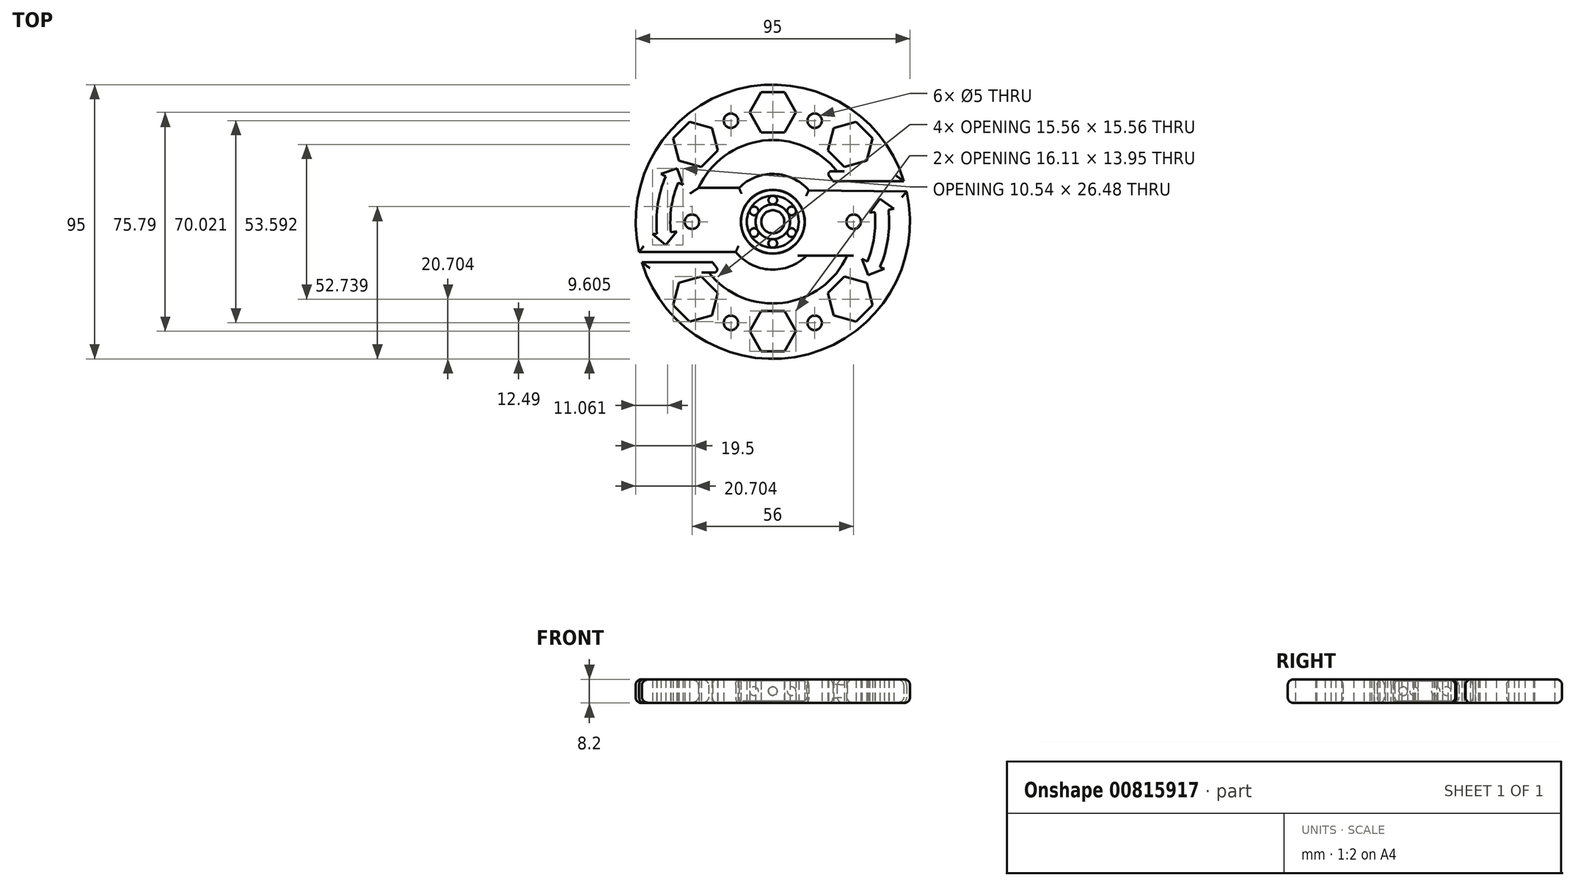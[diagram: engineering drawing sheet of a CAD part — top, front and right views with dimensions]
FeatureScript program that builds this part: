
annotation { "Feature Type Name" : "Feature", "Feature Type Description" : "" }
export const myFeature = defineFeature(function(context is Context, id is Id, definition is map)
    precondition{}
    {
        {
            var Q0;
            Q0=qCreatedBy(makeId("Top.planeOp"),FACE);
            var sketch = newSketch(context, id + "F0", { "sketchPlane" : qUnion([Q0])});
            skArc(sketch, "E0", {"start": v(45.38, 14.04) * mm, "mid": v(-10.46, 46.33) * mm, "end": v(-47, -6.81) * mm});
            skLineSegment(sketch, "E1.top", {"start": v(-45.38, -14.04) * mm, "end": v(-24.56, -14.04) * mm});
            skCircle(sketch, "E2", {"center": v(0, 0) * mm, "radius": 11.07 * mm});
            skArc(sketch, "E3", {"start": v(22.24, 17.5) * mm, "mid": v(-3.38, 28.09) * mm, "end": v(-25.75, 11.72) * mm});
            skArc(sketch, "E4.trimOffspring", {"start": v(-22.2, -17.54) * mm, "mid": v(3.4, -28.08) * mm, "end": v(25.75, -11.72) * mm});
            skArc(sketch, "E5.trimOffspring", {"start": v(-45.38, -14.04) * mm, "mid": v(10.5, -46.32) * mm, "end": v(47, 6.9) * mm});
            skLineSegment(sketch, "E6.trimOffspring", {"start": v(24.59, 14) * mm, "end": v(45.38, 14.04) * mm});
            skPoint(sketch, "E7.trimOffspring.end.orphan", {"position": v(45.38, -14.04) * mm});
            skPoint(sketch, "E1.bottom.start.orphan", {"position": v(-45.38, 14.04) * mm});
            skPoint(sketch, "E8.orphan", {"position": v(47, -6.9) * mm});
            skPoint(sketch, "E9.orphan", {"position": v(-47, 6.81) * mm});
            skArc(sketch, "E10", {"start": v(-12.86, -10.46) * mm, "mid": v(-0.85, -16.55) * mm, "end": v(11.72, -11.72) * mm});
            skArc(sketch, "E11.trimOffspring", {"start": v(12.47, 10.92) * mm, "mid": v(0.55, 16.57) * mm, "end": v(-11.72, 11.72) * mm});
            skLineSegment(sketch, "E12.trimOffspring", {"start": v(-8.7, 6.85) * mm, "end": v(8.59, 7) * mm});
            skLineSegment(sketch, "E13.trimOffspring", {"start": v(-8.7, -6.85) * mm, "end": v(8.69, -6.87) * mm});
            skLineSegment(sketch, "E14", {"start": v(-7.83, 7.83) * mm, "end": v(-6.87, 6.87) * mm});
            skLineSegment(sketch, "E15", {"start": v(6.87, -6.87) * mm, "end": v(7.83, -7.83) * mm});
            skLineSegment(sketch, "E16", {"start": v(-11.72, 11.72) * mm, "end": v(-25.75, 11.72) * mm});
            skLineSegment(sketch, "E17", {"start": v(11.72, -11.72) * mm, "end": v(11.72, -11.72) * mm});
            skArc(sketch, "E18", {"start": v(20.88, 14) * mm, "mid": v(19.54, 15.8) * mm, "end": v(18.05, 17.5) * mm});
            skLineSegment(sketch, "E19", {"start": v(-24.56, -14.04) * mm, "end": v(-20.85, -14.04) * mm});
            skLineSegment(sketch, "E20", {"start": v(24.59, 14) * mm, "end": v(20.88, 14) * mm});
            skLineSegment(sketch, "E21", {"start": v(22.24, 17.5) * mm, "end": v(18.05, 17.5) * mm});
            skLineSegment(sketch, "E22", {"start": v(-22.2, -17.54) * mm, "end": v(-18, -17.54) * mm});
            skArc(sketch, "E23.trimOffspring", {"start": v(-20.85, -14.04) * mm, "mid": v(-19.5, -15.85) * mm, "end": v(-18, -17.54) * mm});
            skLineSegment(sketch, "E24", {"start": v(0, 0) * mm, "end": v(0, 16.57) * mm, "construction": true});
            skLineSegment(sketch, "E25", {"start": v(-6.87, 6.87) * mm, "end": v(-11.72, 11.72) * mm, "construction": true});
            skLineSegment(sketch, "E26", {"start": v(0, 0) * mm, "end": v(11.72, 11.72) * mm, "construction": true});
            skLineSegment(sketch, "E27", {"start": v(6.87, -6.87) * mm, "end": v(11.72, -11.72) * mm, "construction": true});
            skLineSegment(sketch, "E28", {"start": v(0, 0) * mm, "end": v(0, -16.57) * mm, "construction": true});
            skLineSegment(sketch, "E29", {"start": v(0, 0) * mm, "end": v(-11.72, -11.72) * mm, "construction": true});
            skLineSegment(sketch, "E30.trimOffspring", {"start": v(-20, 20) * mm, "end": v(-33.59, 33.59) * mm, "construction": true});
            skLineSegment(sketch, "E31.trimOffspring", {"start": v(0, 28.29) * mm, "end": v(0, 47.5) * mm, "construction": true});
            skLineSegment(sketch, "E32.trimOffspring", {"start": v(20, 20) * mm, "end": v(33.59, 33.59) * mm, "construction": true});
            skLineSegment(sketch, "E33.trimOffspring", {"start": v(20, -20) * mm, "end": v(33.59, -33.59) * mm, "construction": true});
            skLineSegment(sketch, "E34.trimOffspring", {"start": v(0, -28.29) * mm, "end": v(0, -47.5) * mm, "construction": true});
            skLineSegment(sketch, "E35.trimOffspring", {"start": v(-20, -20) * mm, "end": v(-33.59, -33.59) * mm, "construction": true});
            skPoint(sketch, "E36", {"position": v(0, 37.9) * mm});
            skPoint(sketch, "E37", {"position": v(-26.8, 26.8) * mm});
            skPoint(sketch, "E38", {"position": v(26.8, 26.8) * mm});
            skPoint(sketch, "E39", {"position": v(26.8, -26.8) * mm});
            skPoint(sketch, "E40", {"position": v(0, -37.9) * mm});
            skPoint(sketch, "E41", {"position": v(-26.8, -26.8) * mm});
            skLineSegment(sketch, "E42.0", {"start": v(-32.5, 21.1) * mm, "end": v(-34.58, 28.88) * mm});
            skLineSegment(sketch, "E42.1", {"start": v(-34.58, 28.88) * mm, "end": v(-28.88, 34.58) * mm});
            skLineSegment(sketch, "E42.2", {"start": v(-28.88, 34.58) * mm, "end": v(-21.1, 32.5) * mm});
            skLineSegment(sketch, "E42.3", {"start": v(-21.1, 32.5) * mm, "end": v(-19.02, 24.71) * mm});
            skLineSegment(sketch, "E42.4", {"start": v(-19.02, 24.71) * mm, "end": v(-24.71, 19.02) * mm});
            skLineSegment(sketch, "E42.5", {"start": v(-24.71, 19.02) * mm, "end": v(-32.5, 21.1) * mm});
            skLineSegment(sketch, "E43.0", {"start": v(21.1, -32.5) * mm, "end": v(19.02, -24.71) * mm});
            skLineSegment(sketch, "E43.1", {"start": v(19.02, -24.71) * mm, "end": v(24.71, -19.02) * mm});
            skLineSegment(sketch, "E43.2", {"start": v(24.71, -19.02) * mm, "end": v(32.5, -21.1) * mm});
            skLineSegment(sketch, "E43.3", {"start": v(32.5, -21.1) * mm, "end": v(34.58, -28.88) * mm});
            skLineSegment(sketch, "E43.4", {"start": v(34.58, -28.88) * mm, "end": v(28.88, -34.58) * mm});
            skLineSegment(sketch, "E43.5", {"start": v(28.88, -34.58) * mm, "end": v(21.1, -32.5) * mm});
            skLineSegment(sketch, "E44.0", {"start": v(-8.05, 37.9) * mm, "end": v(-4.03, 44.87) * mm});
            skLineSegment(sketch, "E44.1", {"start": v(-4.03, 44.87) * mm, "end": v(4.03, 44.87) * mm});
            skLineSegment(sketch, "E44.2", {"start": v(4.03, 44.87) * mm, "end": v(8.05, 37.9) * mm});
            skLineSegment(sketch, "E44.3", {"start": v(8.05, 37.9) * mm, "end": v(4.03, 30.92) * mm});
            skLineSegment(sketch, "E44.4", {"start": v(4.03, 30.92) * mm, "end": v(-4.03, 30.92) * mm});
            skLineSegment(sketch, "E44.5", {"start": v(-4.03, 30.92) * mm, "end": v(-8.05, 37.9) * mm});
            skLineSegment(sketch, "E45.0", {"start": v(-8.05, -37.9) * mm, "end": v(-4.03, -30.92) * mm});
            skLineSegment(sketch, "E45.1", {"start": v(-4.03, -30.92) * mm, "end": v(4.03, -30.92) * mm});
            skLineSegment(sketch, "E45.2", {"start": v(4.03, -30.92) * mm, "end": v(8.05, -37.9) * mm});
            skLineSegment(sketch, "E45.3", {"start": v(8.05, -37.9) * mm, "end": v(4.03, -44.87) * mm});
            skLineSegment(sketch, "E45.4", {"start": v(4.03, -44.87) * mm, "end": v(-4.03, -44.87) * mm});
            skLineSegment(sketch, "E45.5", {"start": v(-4.03, -44.87) * mm, "end": v(-8.05, -37.9) * mm});
            skLineSegment(sketch, "E46.0", {"start": v(-32.5, -21.1) * mm, "end": v(-24.71, -19.02) * mm});
            skLineSegment(sketch, "E46.1", {"start": v(-24.71, -19.02) * mm, "end": v(-19.02, -24.71) * mm});
            skLineSegment(sketch, "E46.2", {"start": v(-19.02, -24.71) * mm, "end": v(-21.1, -32.5) * mm});
            skLineSegment(sketch, "E46.3", {"start": v(-21.1, -32.5) * mm, "end": v(-28.88, -34.58) * mm});
            skLineSegment(sketch, "E46.4", {"start": v(-28.88, -34.58) * mm, "end": v(-34.58, -28.88) * mm});
            skLineSegment(sketch, "E46.5", {"start": v(-34.58, -28.88) * mm, "end": v(-32.5, -21.1) * mm});
            skLineSegment(sketch, "E47.0", {"start": v(21.1, 32.5) * mm, "end": v(28.88, 34.58) * mm});
            skLineSegment(sketch, "E47.1", {"start": v(28.88, 34.58) * mm, "end": v(34.58, 28.88) * mm});
            skLineSegment(sketch, "E47.2", {"start": v(34.58, 28.88) * mm, "end": v(32.5, 21.1) * mm});
            skLineSegment(sketch, "E47.3", {"start": v(32.5, 21.1) * mm, "end": v(24.71, 19.02) * mm});
            skLineSegment(sketch, "E47.4", {"start": v(24.71, 19.02) * mm, "end": v(19.02, 24.71) * mm});
            skLineSegment(sketch, "E47.5", {"start": v(19.02, 24.71) * mm, "end": v(21.1, 32.5) * mm});
            skArc(sketch, "E48", {"start": v(-45.38, -14.04) * mm, "mid": v(10.5, -46.32) * mm, "end": v(47, 6.9) * mm, "construction": true});
            skArc(sketch, "E49", {"start": v(-47, -6.81) * mm, "mid": v(-46.7, -8.64) * mm, "end": v(-46.33, -10.46) * mm});
            skPoint(sketch, "E50", {"position": v(-46.33, -10.46) * mm});
            skArc(sketch, "E51", {"start": v(45.38, 14.04) * mm, "mid": v(-10.46, 46.33) * mm, "end": v(-47, -6.81) * mm, "construction": true});
            skArc(sketch, "E52", {"start": v(47, 6.9) * mm, "mid": v(46.7, 8.71) * mm, "end": v(46.32, 10.5) * mm});
            skPoint(sketch, "E53", {"position": v(46.32, 10.5) * mm});
            skLineSegment(sketch, "E54", {"start": v(-46.33, -10.46) * mm, "end": v(-36.42, -10.46) * mm});
            skLineSegment(sketch, "E55", {"start": v(46.32, 10.5) * mm, "end": v(12.47, 10.92) * mm});
            skPoint(sketch, "E56", {"position": v(-114.88, 3.23) * mm});
            skLineSegment(sketch, "E57.0", {"start": v(-114.88, 9.7) * mm, "end": v(-109.28, 6.47) * mm});
            skLineSegment(sketch, "E57.1", {"start": v(-109.28, 6.47) * mm, "end": v(-109.28, 0) * mm});
            skLineSegment(sketch, "E57.2", {"start": v(-109.28, 0) * mm, "end": v(-114.88, -3.23) * mm});
            skLineSegment(sketch, "E57.3", {"start": v(-114.88, -3.23) * mm, "end": v(-120.48, 0) * mm});
            skLineSegment(sketch, "E57.4", {"start": v(-120.48, 0) * mm, "end": v(-120.48, 6.47) * mm});
            skLineSegment(sketch, "E57.5", {"start": v(-120.48, 6.47) * mm, "end": v(-114.88, 9.7) * mm});
            skPoint(sketch, "E58", {"position": v(-130.27, -23) * mm});
            skLineSegment(sketch, "E59.0", {"start": v(-130.27, -16.53) * mm, "end": v(-124.67, -19.77) * mm});
            skLineSegment(sketch, "E59.1", {"start": v(-124.67, -19.77) * mm, "end": v(-124.67, -26.23) * mm});
            skLineSegment(sketch, "E59.2", {"start": v(-124.67, -26.23) * mm, "end": v(-130.27, -29.47) * mm});
            skLineSegment(sketch, "E59.3", {"start": v(-130.27, -29.47) * mm, "end": v(-135.87, -26.23) * mm});
            skLineSegment(sketch, "E59.4", {"start": v(-135.87, -26.23) * mm, "end": v(-135.87, -19.77) * mm});
            skLineSegment(sketch, "E59.5", {"start": v(-135.87, -19.77) * mm, "end": v(-130.27, -16.53) * mm});
            skLineSegment(sketch, "E60", {"start": v(-11.07, 0) * mm, "end": v(-47.5, 0) * mm, "construction": true});
            skLineSegment(sketch, "E61", {"start": v(11.07, 0) * mm, "end": v(47.5, 0) * mm, "construction": true});
            skLineSegment(sketch, "E62.0", {"start": v(-137.37, -18.9) * mm, "end": v(-130.27, -14.8) * mm});
            skLineSegment(sketch, "E62.1", {"start": v(-123.17, -18.9) * mm, "end": v(-123.17, -27.1) * mm});
            skLineSegment(sketch, "E62.2", {"start": v(-123.17, -27.1) * mm, "end": v(-130.27, -31.2) * mm});
            skLineSegment(sketch, "E62.3", {"start": v(-130.27, -14.8) * mm, "end": v(-123.17, -18.9) * mm});
            skLineSegment(sketch, "E62.4", {"start": v(-130.27, -31.2) * mm, "end": v(-137.37, -27.1) * mm});
            skLineSegment(sketch, "E62.5", {"start": v(-137.37, -27.1) * mm, "end": v(-137.37, -18.9) * mm});
            skLineSegment(sketch, "E63.0", {"start": v(-138.87, -18.03) * mm, "end": v(-130.27, -13.07) * mm});
            skLineSegment(sketch, "E63.1", {"start": v(-121.67, -18.03) * mm, "end": v(-121.67, -27.97) * mm});
            skLineSegment(sketch, "E63.2", {"start": v(-121.67, -27.97) * mm, "end": v(-130.27, -32.93) * mm});
            skLineSegment(sketch, "E63.3", {"start": v(-130.27, -13.07) * mm, "end": v(-121.67, -18.03) * mm});
            skLineSegment(sketch, "E63.4", {"start": v(-130.27, -32.93) * mm, "end": v(-138.87, -27.97) * mm});
            skLineSegment(sketch, "E63.5", {"start": v(-138.87, -27.97) * mm, "end": v(-138.87, -18.03) * mm});
            skPoint(sketch, "E64", {"position": v(-99.9, -24.26) * mm});
            skLineSegment(sketch, "E65.0", {"start": v(-109.83, -24.26) * mm, "end": v(-104.87, -15.66) * mm});
            skLineSegment(sketch, "E65.1", {"start": v(-94.94, -15.66) * mm, "end": v(-89.97, -24.26) * mm});
            skLineSegment(sketch, "E65.2", {"start": v(-89.97, -24.26) * mm, "end": v(-94.94, -32.86) * mm});
            skLineSegment(sketch, "E65.3", {"start": v(-104.87, -15.66) * mm, "end": v(-94.94, -15.66) * mm});
            skLineSegment(sketch, "E65.4", {"start": v(-94.94, -32.86) * mm, "end": v(-104.87, -32.86) * mm});
            skLineSegment(sketch, "E65.5", {"start": v(-104.87, -32.86) * mm, "end": v(-109.83, -24.26) * mm});
            skLineSegment(sketch, "E66.0", {"start": v(-107.82, -22.14) * mm, "end": v(-102.03, -16.34) * mm});
            skLineSegment(sketch, "E66.1", {"start": v(-94.1, -18.47) * mm, "end": v(-91.98, -26.38) * mm});
            skLineSegment(sketch, "E66.2", {"start": v(-91.98, -26.38) * mm, "end": v(-97.78, -32.18) * mm});
            skLineSegment(sketch, "E66.3", {"start": v(-102.03, -16.34) * mm, "end": v(-94.1, -18.47) * mm});
            skLineSegment(sketch, "E66.4", {"start": v(-97.78, -32.18) * mm, "end": v(-105.7, -30.06) * mm});
            skLineSegment(sketch, "E66.5", {"start": v(-105.7, -30.06) * mm, "end": v(-107.82, -22.14) * mm});
            skLineSegment(sketch, "E67.0", {"start": v(-99.9, -17.8) * mm, "end": v(-94.3, -21.03) * mm});
            skLineSegment(sketch, "E67.1", {"start": v(-94.3, -21.03) * mm, "end": v(-94.3, -27.5) * mm});
            skLineSegment(sketch, "E67.2", {"start": v(-94.3, -27.5) * mm, "end": v(-99.9, -30.73) * mm});
            skLineSegment(sketch, "E67.3", {"start": v(-99.9, -30.73) * mm, "end": v(-105.5, -27.5) * mm});
            skLineSegment(sketch, "E67.4", {"start": v(-105.5, -27.5) * mm, "end": v(-105.5, -21.03) * mm});
            skLineSegment(sketch, "E67.5", {"start": v(-105.5, -21.03) * mm, "end": v(-99.9, -17.8) * mm});
            skLineSegment(sketch, "E68.0", {"start": v(-111.57, -24.26) * mm, "end": v(-105.73, -14.16) * mm});
            skLineSegment(sketch, "E68.1", {"start": v(-94.07, -14.16) * mm, "end": v(-88.24, -24.26) * mm});
            skLineSegment(sketch, "E68.2", {"start": v(-88.24, -24.26) * mm, "end": v(-94.07, -34.36) * mm});
            skLineSegment(sketch, "E68.3", {"start": v(-105.73, -14.16) * mm, "end": v(-94.07, -14.16) * mm});
            skLineSegment(sketch, "E68.4", {"start": v(-94.07, -34.36) * mm, "end": v(-105.73, -34.36) * mm});
            skLineSegment(sketch, "E68.5", {"start": v(-105.73, -34.36) * mm, "end": v(-111.57, -24.26) * mm});
            skArc(sketch, "E69", {"start": v(-12.86, -10.46) * mm, "mid": v(16.55, -0.85) * mm, "end": v(-11.72, 11.72) * mm, "construction": true});
            skArc(sketch, "E70", {"start": v(-11.72, 11.72) * mm, "mid": v(-16.55, 0.85) * mm, "end": v(-12.86, -10.46) * mm, "construction": true});
            skLineSegment(sketch, "E71", {"start": v(11.72, -11.72) * mm, "end": v(25.75, -11.72) * mm});
            skLineSegment(sketch, "E72", {"start": v(12.47, 10.92) * mm, "end": v(12.47, 10.92) * mm});
            skCircle(sketch, "E73", {"center": v(-28, 0) * mm, "radius": 2.5 * mm});
            skCircle(sketch, "E74.MirrorC", {"center": v(28, 0) * mm, "radius": 2.5 * mm});
            skArc(sketch, "E75", {"start": v(-20.87, 31.63) * mm, "mid": v(-26.8, 26.8) * mm, "end": v(-31.63, 20.87) * mm, "construction": true});
            skArc(sketch, "E76", {"start": v(-7.6, 37.12) * mm, "mid": v(-14.5, 35.01) * mm, "end": v(-20.87, 31.63) * mm, "construction": true});
            skArc(sketch, "E77", {"start": v(7.6, 37.12) * mm, "mid": v(0, 37.9) * mm, "end": v(-7.6, 37.12) * mm, "construction": true});
            skArc(sketch, "E78", {"start": v(20.87, 31.63) * mm, "mid": v(14.5, 35.01) * mm, "end": v(7.6, 37.12) * mm, "construction": true});
            skCircle(sketch, "E79", {"center": v(-14.5, 35.01) * mm, "radius": 2.5 * mm});
            skCircle(sketch, "E80", {"center": v(14.5, 35.01) * mm, "radius": 2.5 * mm});
            skCircle(sketch, "E81.MirrorC", {"center": v(-14.5, -35.01) * mm, "radius": 2.5 * mm});
            skCircle(sketch, "E82.MirrorC", {"center": v(14.5, -35.01) * mm, "radius": 2.5 * mm});
            skLineSegment(sketch, "E83", {"start": v(-31.63, 20.87) * mm, "end": v(-31.63, 20.87) * mm});
            skLineSegment(sketch, "E84", {"start": v(-36.42, -10.46) * mm, "end": v(-12.86, -10.46) * mm});
            skPoint(sketch, "E85", {"position": v(-31.63, 20.87) * mm});
            skPoint(sketch, "E86", {"position": v(-36.42, -10.46) * mm});
            skArc(sketch, "E87", {"start": v(-31.63, 20.87) * mm, "mid": v(-37.46, 5.73) * mm, "end": v(-36.42, -10.46) * mm, "construction": true});
            skArc(sketch, "E88", {"start": v(-36.42, -10.46) * mm, "mid": v(22.43, -30.54) * mm, "end": v(20.87, 31.63) * mm, "construction": true});
            skArc(sketch, "E89.0", {"start": v(-37.1, 15.73) * mm, "mid": v(-39.84, 6.03) * mm, "end": v(-40.1, -4.06) * mm});
            skArc(sketch, "E90.0", {"start": v(-32.79, 13.6) * mm, "mid": v(-35.12, 5.18) * mm, "end": v(-35.32, -3.55) * mm});
            skPoint(sketch, "E91", {"position": v(-33.09, 18.48) * mm});
            skPoint(sketch, "E92", {"position": v(-37.04, -8) * mm});
            skLineSegment(sketch, "E93", {"start": v(-37.04, -8) * mm, "end": v(-33.27, -3.33) * mm});
            skLineSegment(sketch, "E94", {"start": v(-37.04, -8) * mm, "end": v(-41.7, -4.23) * mm});
            skLineSegment(sketch, "E95", {"start": v(-41.7, -4.23) * mm, "end": v(-40.1, -4.06) * mm});
            skLineSegment(sketch, "E96.trimOffspring", {"start": v(-35.32, -3.55) * mm, "end": v(-33.27, -3.33) * mm});
            skLineSegment(sketch, "E97", {"start": v(-33.09, 18.48) * mm, "end": v(-38.77, 16.56) * mm});
            skLineSegment(sketch, "E98", {"start": v(-33.09, 18.48) * mm, "end": v(-31.17, 12.8) * mm});
            skLineSegment(sketch, "E99", {"start": v(-31.17, 12.8) * mm, "end": v(-32.79, 13.6) * mm});
            skLineSegment(sketch, "E100.trimOffspring", {"start": v(-37.1, 15.73) * mm, "end": v(-38.77, 16.56) * mm});
            skArc(sketch, "E101.MirrorCS", {"start": v(35.33, 3.39) * mm, "mid": v(35.1, -5.34) * mm, "end": v(32.73, -13.74) * mm});
            skArc(sketch, "E102.MirrorCS", {"start": v(40.08, 4.17) * mm, "mid": v(39.86, -5.91) * mm, "end": v(37.14, -15.63) * mm});
            skLineSegment(sketch, "E103.MirrorCS", {"start": v(33.07, -18.5) * mm, "end": v(38.64, -16.27) * mm});
            skLineSegment(sketch, "E104.MirrorCS", {"start": v(33.07, -18.5) * mm, "end": v(30.83, -12.94) * mm});
            skPoint(sketch, "E105.MirrorP", {"position": v(33.07, -18.5) * mm});
            skLineSegment(sketch, "E106.MirrorCS", {"start": v(37.05, 7.97) * mm, "end": v(33.55, 3.1) * mm});
            skLineSegment(sketch, "E107.MirrorCS", {"start": v(37.05, 7.97) * mm, "end": v(41.92, 4.47) * mm});
            skPoint(sketch, "E108.MirrorP", {"position": v(37.05, 7.97) * mm});
            skLineSegment(sketch, "E109.MirrorCS", {"start": v(40.08, 4.17) * mm, "end": v(41.92, 4.47) * mm});
            skLineSegment(sketch, "E110.MirrorCS", {"start": v(33.55, 3.1) * mm, "end": v(35.33, 3.39) * mm});
            skLineSegment(sketch, "E111.MirrorCS", {"start": v(32.73, -13.74) * mm, "end": v(30.83, -12.94) * mm});
            skLineSegment(sketch, "E112.MirrorCS", {"start": v(38.64, -16.27) * mm, "end": v(37.14, -15.63) * mm});
            skSolve(sketch);
        }
        {
            var Q0;
            Q0=makeQuery(id+"F0.imprint","IMPRINT",FACE,{"disambiguationData":[TD([[makeQuery(id+"F0.imprint","IMPRINT",EDGE,{"derivedFrom":sQuery(id+"F0.wireOp",EDGE,"E0")}),1.0]])]});
            extrude(context, id + "F1", {"entities" : qUnion([Q0]), "endBound" : BoundingType.SYMMETRIC, "depth" : 8.2 * mm, "offsetDistance" : 25 * mm});
        }
        {
            var Q0;
            Q0=makeQuery(id+"F1.opExtrude","CAP_EDGE",EDGE,{"disambiguationData":[OSD([sQuery(id+"F0.wireOp",EDGE,"E0")])],"isStart":false});
            var Q1;
            Q1=makeQuery(id+"F1.opExtrude","CAP_EDGE",EDGE,{"disambiguationData":[OSD([sQuery(id+"F0.wireOp",EDGE,"E5.trimOffspring")])],"isStart":false});
            var Q2;
            Q2=makeQuery(id+"F1.opExtrude","CAP_EDGE",EDGE,{"disambiguationData":[OSD([sQuery(id+"F0.wireOp",EDGE,"E0")])],"isStart":true});
            var Q3;
            Q3=makeQuery(id+"F1.opExtrude","CAP_EDGE",EDGE,{"disambiguationData":[OSD([sQuery(id+"F0.wireOp",EDGE,"E5.trimOffspring")])],"isStart":true});
            var Q4;
            Q4=makeQuery(id+"F1.opExtrude","CAP_EDGE",EDGE,{"disambiguationData":[OSD([sQuery(id+"F0.wireOp",EDGE,"E1.top"),sQuery(id+"F0.wireOp",EDGE,"E19")])],"isStart":true});
            var Q5;
            Q5=makeQuery(id+"F1.opExtrude","CAP_EDGE",EDGE,{"disambiguationData":[OSD([sQuery(id+"F0.wireOp",EDGE,"E1.top"),sQuery(id+"F0.wireOp",EDGE,"E19")])],"isStart":false});
            var Q6;
            Q6=makeQuery(id+"F1.opExtrude","CAP_EDGE",EDGE,{"disambiguationData":[OSD([sQuery(id+"F0.wireOp",EDGE,"af73f036-c247-4c71-b03d-1512b0a657ec.trimOffspring")])],"isStart":true});
            var Q7;
            Q7=makeQuery(id+"F1.opExtrude","CAP_EDGE",EDGE,{"disambiguationData":[OSD([sQuery(id+"F0.wireOp",EDGE,"af73f036-c247-4c71-b03d-1512b0a657ec.trimOffspring")])],"isStart":false});
            var Q8;
            Q8=makeQuery(id+"F1.opExtrude","CAP_EDGE",EDGE,{"disambiguationData":[OSD([sQuery(id+"F0.wireOp",EDGE,"E11.trimOffspring")])],"isStart":false});
            var Q9;
            Q9=makeQuery(id+"F1.opExtrude","CAP_EDGE",EDGE,{"disambiguationData":[OSD([sQuery(id+"F0.wireOp",EDGE,"E11.trimOffspring")])],"isStart":true});
            var Q10;
            Q10=makeQuery(id+"F1.opExtrude","CAP_EDGE",EDGE,{"disambiguationData":[OSD([sQuery(id+"F0.wireOp",EDGE,"E16")])],"isStart":false});
            var Q11;
            Q11=makeQuery(id+"F1.opExtrude","CAP_EDGE",EDGE,{"disambiguationData":[OSD([sQuery(id+"F0.wireOp",EDGE,"E16")])],"isStart":true});
            var Q12;
            Q12=makeQuery(id+"F1.opExtrude","CAP_EDGE",EDGE,{"disambiguationData":[OSD([sQuery(id+"F0.wireOp",EDGE,"E4.trimOffspring")])],"isStart":true});
            var Q13;
            Q13=makeQuery(id+"F1.opExtrude","CAP_EDGE",EDGE,{"disambiguationData":[OSD([sQuery(id+"F0.wireOp",EDGE,"E4.trimOffspring")])],"isStart":false});
            var Q14;
            Q14=makeQuery(id+"F1.opExtrude","CAP_EDGE",EDGE,{"disambiguationData":[OSD([sQuery(id+"F0.wireOp",EDGE,"E3")])],"isStart":false});
            var Q15;
            Q15=makeQuery(id+"F1.opExtrude","CAP_EDGE",EDGE,{"disambiguationData":[OSD([sQuery(id+"F0.wireOp",EDGE,"E3")])],"isStart":true});
            var Q16;
            Q16=makeQuery(id+"F1.opExtrude","CAP_EDGE",EDGE,{"disambiguationData":[OSD([sQuery(id+"F0.wireOp",EDGE,"E17")])],"isStart":false});
            var Q17;
            Q17=makeQuery(id+"F1.opExtrude","CAP_EDGE",EDGE,{"disambiguationData":[OSD([sQuery(id+"F0.wireOp",EDGE,"E17")])],"isStart":true});
            var Q18;
            Q18=makeQuery(id+"F1.opExtrude","CAP_EDGE",EDGE,{"disambiguationData":[OSD([sQuery(id+"F0.wireOp",EDGE,"E10")])],"isStart":false});
            var Q19;
            Q19=makeQuery(id+"F1.opExtrude","CAP_EDGE",EDGE,{"disambiguationData":[OSD([sQuery(id+"F0.wireOp",EDGE,"E10")])],"isStart":true});
            var Q20;
            Q20=makeQuery(id+"F1.opExtrude","CAP_EDGE",EDGE,{"disambiguationData":[OSD([sQuery(id+"F0.wireOp",EDGE,"318f1a37-417c-41ab-8845-f020125537680.MirrorCS")])],"isStart":false});
            var Q21;
            Q21=makeQuery(id+"F1.opExtrude","CAP_EDGE",EDGE,{"disambiguationData":[OSD([sQuery(id+"F0.wireOp",EDGE,"318f1a37-417c-41ab-8845-f020125537680.MirrorCS")])],"isStart":true});
            var Q22;
            Q22=makeQuery(id+"F1.opExtrude","CAP_EDGE",EDGE,{"disambiguationData":[OSD([sQuery(id+"F0.wireOp",EDGE,"E6.trimOffspring")])],"isStart":false});
            var Q23;
            Q23=makeQuery(id+"F1.opExtrude","CAP_EDGE",EDGE,{"disambiguationData":[OSD([sQuery(id+"F0.wireOp",EDGE,"E6.trimOffspring")])],"isStart":true});
            var Q24;
            Q24=makeQuery(id+"F1.opExtrude","CAP_EDGE",EDGE,{"disambiguationData":[OSD([sQuery(id+"F0.wireOp",EDGE,"E54")])],"isStart":false});
            var Q25;
            Q25=makeQuery(id+"F1.opExtrude","CAP_EDGE",EDGE,{"disambiguationData":[OSD([sQuery(id+"F0.wireOp",EDGE,"E54")])],"isStart":true});
            var Q26;
            Q26=makeQuery(id+"F1.opExtrude","CAP_EDGE",EDGE,{"disambiguationData":[OSD([sQuery(id+"F0.wireOp",EDGE,"E55")])],"isStart":true});
            var Q27;
            Q27=makeQuery(id+"F1.opExtrude","CAP_EDGE",EDGE,{"disambiguationData":[OSD([sQuery(id+"F0.wireOp",EDGE,"E55")])],"isStart":false});
            fillet(context, id + "F2", {"entities" : qUnion([Q0, Q1, Q2, Q3, Q4, Q5, Q6, Q7, Q8, Q9, Q10, Q11, Q12, Q13, Q14, Q15, Q16, Q17, Q18, Q19, Q20, Q21, Q22, Q23, Q24, Q25, Q26, Q27]), "radius" : 2 * mm, "tangentPropagation" : true, "allowEdgeOverflow" : false});
        }
        {
            var Q0;
            Q0=qCreatedBy(makeId("Top.planeOp"),FACE);
            var sketch = newSketch(context, id + "F3", { "sketchPlane" : qUnion([Q0])});
            skCircle(sketch, "E113", {"center": v(56.9, -63.65) * mm, "radius": 11 * mm});
            skCircle(sketch, "E114", {"center": v(56.9, -63.65) * mm, "radius": 9 * mm});
            skCircle(sketch, "E115", {"center": v(56.9, -63.65) * mm, "radius": 4 * mm});
            skCircle(sketch, "E116", {"center": v(56.9, -63.65) * mm, "radius": 6 * mm});
            skArc(sketch, "E117", {"start": v(56.9, -57.65) * mm, "mid": v(58.4, -56.15) * mm, "end": v(56.9, -54.65) * mm});
            skArc(sketch, "E118.1.0", {"start": v(63.4, -61.4) * mm, "mid": v(64.9, -59.9) * mm, "end": v(63.4, -58.4) * mm});
            skArc(sketch, "E118.2.0", {"start": v(63.4, -68.9) * mm, "mid": v(64.9, -67.4) * mm, "end": v(63.4, -65.9) * mm});
            skArc(sketch, "E118.3.0", {"start": v(56.9, -72.65) * mm, "mid": v(58.4, -71.14) * mm, "end": v(56.88, -69.65) * mm});
            skArc(sketch, "E118.4.0", {"start": v(50.41, -68.9) * mm, "mid": v(51.91, -67.4) * mm, "end": v(50.41, -65.9) * mm});
            skArc(sketch, "E118.5.0", {"start": v(50.41, -61.4) * mm, "mid": v(51.91, -59.9) * mm, "end": v(50.41, -58.4) * mm});
            skLineSegment(sketch, "E119", {"start": v(50.41, -65.9) * mm, "end": v(50.41, -68.9) * mm});
            skLineSegment(sketch, "E120", {"start": v(56.88, -69.65) * mm, "end": v(56.9, -72.65) * mm});
            skLineSegment(sketch, "E121", {"start": v(63.4, -65.9) * mm, "end": v(63.4, -68.9) * mm});
            skLineSegment(sketch, "E122", {"start": v(63.4, -58.4) * mm, "end": v(63.4, -61.4) * mm});
            skLineSegment(sketch, "E123", {"start": v(56.9, -54.65) * mm, "end": v(56.9, -54.65) * mm});
            skLineSegment(sketch, "E124", {"start": v(50.41, -58.4) * mm, "end": v(50.41, -61.4) * mm});
            skLineSegment(sketch, "E125.trimOffspring", {"start": v(56.9, -57.65) * mm, "end": v(56.9, -57.65) * mm});
            skLineSegment(sketch, "E126.trimOffspring", {"start": v(51.71, -60.65) * mm, "end": v(51.71, -60.65) * mm});
            skLineSegment(sketch, "E127", {"start": v(56.9, -57.65) * mm, "end": v(56.9, -54.65) * mm});
            skSolve(sketch);
        }
        {
            var Q0;
            Q0=makeQuery(id+"F3.imprint","IMPRINT",FACE,{"disambiguationData":[TD([[makeQuery(id+"F3.imprint","IMPRINT",EDGE,{"derivedFrom":sQuery(id+"F3.wireOp",EDGE,"E113")}),1.0]])]});
            var Q1;
            Q1=makeQuery(id+"F3.imprint","IMPRINT",FACE,{"disambiguationData":[TD([[makeQuery(id+"F3.imprint","IMPRINT",EDGE,{"derivedFrom":sQuery(id+"F3.wireOp",EDGE,"E115")}),-1.0]])]});
            extrude(context, id + "F4", {"entities" : qUnion([Q0, Q1]), "endBound" : BoundingType.SYMMETRIC, "depth" : 7 * mm, "offsetDistance" : 25 * mm});
        }
        {
            var Q0;
            Q0=makeQuery(id+"F3.imprint","IMPRINT",FACE,{"disambiguationData":[TD([[makeQuery(id+"F3.imprint","IMPRINT",EDGE,{"derivedFrom":sQuery(id+"F3.wireOp",EDGE,"E117")}),1.0]])]});
            var Q1;
            Q1=sQuery(id+"F3.wireOp",EDGE,"E127");
            revolve(context, id + "F5", {"surfaceOperationType" : NewSurfaceOperationType.NEW, "entities" : qUnion([Q0]), "axis" : qUnion([Q1]), "revolveType" : RevolveType.FULL});
        }
        {
            var Q0;
            {var subQ0=sQuery(id+"F3.wireOp",EDGE,"E122");Q0=makeQuery(id+"F3.imprint","IMPRINT",FACE,{"disambiguationData":[TD([[makeQuery(id+"F3.imprint","IMPRINT",EDGE,{"derivedFrom":subQ0}),1.0]])]});}
            var Q1;
            Q1=sQuery(id+"F3.wireOp",EDGE,"E122");
            revolve(context, id + "F6", {"surfaceOperationType" : NewSurfaceOperationType.NEW, "entities" : qUnion([Q0]), "axis" : qUnion([Q1]), "revolveType" : RevolveType.FULL});
        }
        {
            var Q0;
            {var subQ0=sQuery(id+"F3.wireOp",EDGE,"E124");Q0=makeQuery(id+"F3.imprint","IMPRINT",FACE,{"disambiguationData":[TD([[makeQuery(id+"F3.imprint","IMPRINT",EDGE,{"derivedFrom":subQ0}),1.0]])]});}
            var Q1;
            Q1=sQuery(id+"F3.wireOp",EDGE,"E124");
            revolve(context, id + "F7", {"surfaceOperationType" : NewSurfaceOperationType.NEW, "entities" : qUnion([Q0]), "axis" : qUnion([Q1]), "revolveType" : RevolveType.FULL});
        }
        {
            var Q0;
            {var subQ0=sQuery(id+"F3.wireOp",EDGE,"E119");Q0=makeQuery(id+"F3.imprint","IMPRINT",FACE,{"disambiguationData":[TD([[makeQuery(id+"F3.imprint","IMPRINT",EDGE,{"derivedFrom":subQ0}),1.0]])]});}
            var Q1;
            Q1=sQuery(id+"F3.wireOp",EDGE,"E119");
            revolve(context, id + "F8", {"surfaceOperationType" : NewSurfaceOperationType.NEW, "entities" : qUnion([Q0]), "axis" : qUnion([Q1]), "revolveType" : RevolveType.FULL});
        }
        {
            var Q0;
            {var subQ0=sQuery(id+"F3.wireOp",EDGE,"E121");Q0=makeQuery(id+"F3.imprint","IMPRINT",FACE,{"disambiguationData":[TD([[makeQuery(id+"F3.imprint","IMPRINT",EDGE,{"derivedFrom":subQ0}),1.0]])]});}
            var Q1;
            Q1=sQuery(id+"F3.wireOp",EDGE,"E121");
            revolve(context, id + "F9", {"surfaceOperationType" : NewSurfaceOperationType.NEW, "entities" : qUnion([Q0]), "axis" : qUnion([Q1]), "revolveType" : RevolveType.FULL});
        }
        {
            var Q0;
            {var subQ0=sQuery(id+"F3.wireOp",EDGE,"E120");Q0=makeQuery(id+"F3.imprint","IMPRINT",FACE,{"disambiguationData":[TD([[makeQuery(id+"F3.imprint","IMPRINT",EDGE,{"derivedFrom":subQ0}),1.0]])]});}
            var Q1;
            Q1=sQuery(id+"F3.wireOp",EDGE,"E120");
            revolve(context, id + "F10", {"surfaceOperationType" : NewSurfaceOperationType.NEW, "entities" : qUnion([Q0]), "axis" : qUnion([Q1]), "revolveType" : RevolveType.FULL});
        }
        {
            var Q0;
            Q0=makeQuery(id+"F6.opRevolve","SWEPT_BODY",BODY,{"disambiguationData":[OSD([sQuery(id+"F3.wireOp",EDGE,"E118.1.0"),sQuery(id+"F3.wireOp",EDGE,"E122")])]});
            var Q1;
            Q1=makeQuery(id+"F5.opRevolve","SWEPT_BODY",BODY,{"disambiguationData":[OSD([sQuery(id+"F3.wireOp",EDGE,"E117"),sQuery(id+"F3.wireOp",EDGE,"E127")])]});
            var Q2;
            Q2=makeQuery(id+"F4.opExtrude","SWEPT_BODY",BODY,{"disambiguationData":[OSD([sQuery(id+"F3.wireOp",EDGE,"E115"),sQuery(id+"F3.wireOp",EDGE,"E116")])]});
            var Q3;
            Q3=makeQuery(id+"F9.opRevolve","SWEPT_BODY",BODY,{"disambiguationData":[OSD([sQuery(id+"F3.wireOp",EDGE,"E118.2.0"),sQuery(id+"F3.wireOp",EDGE,"E121")])]});
            var Q4;
            Q4=makeQuery(id+"F7.opRevolve","SWEPT_BODY",BODY,{"disambiguationData":[OSD([sQuery(id+"F3.wireOp",EDGE,"E118.5.0"),sQuery(id+"F3.wireOp",EDGE,"E124")])]});
            var Q5;
            Q5=makeQuery(id+"F4.opExtrude","SWEPT_BODY",BODY,{"disambiguationData":[OSD([sQuery(id+"F3.wireOp",EDGE,"E113"),sQuery(id+"F3.wireOp",EDGE,"E114")])]});
            var Q6;
            Q6=makeQuery(id+"F10.opRevolve","SWEPT_BODY",BODY,{"disambiguationData":[OSD([sQuery(id+"F3.wireOp",EDGE,"E118.3.0"),sQuery(id+"F3.wireOp",EDGE,"E120")])]});
            var Q7;
            Q7=makeQuery(id+"F8.opRevolve","SWEPT_BODY",BODY,{"disambiguationData":[OSD([sQuery(id+"F3.wireOp",EDGE,"E118.4.0"),sQuery(id+"F3.wireOp",EDGE,"E119")])]});
            transform(context, id + "F11", {"entities" : qUnion([Q0, Q1, Q2, Q3, Q4, Q5, Q6, Q7]), "transformType" : TransformType.TRANSLATION_3D, "dx" : -56.9 * mm, "dy" : 63.65 * mm, "dz" : 0 * mm, "makeCopy" : false});
        }
        {
            var Q0;
            Q0=makeQuery(id+"F1.opExtrude","SWEPT_EDGE",EDGE,{"disambiguationData":[OSD([sQuery(id+"F0.wireOp",EDGE,"E18"),sQuery(id+"F0.wireOp",EDGE,"E21")])]});
            var Q1;
            Q1=makeQuery(id+"F1.opExtrude","SWEPT_EDGE",EDGE,{"disambiguationData":[OSD([sQuery(id+"F0.wireOp",EDGE,"E22"),sQuery(id+"F0.wireOp",EDGE,"E23.trimOffspring")])]});
            fillet(context, id + "F12", {"entities" : qUnion([Q0, Q1]), "radius" : 1 * mm, "tangentPropagation" : true, "allowEdgeOverflow" : false});
        }
    });
